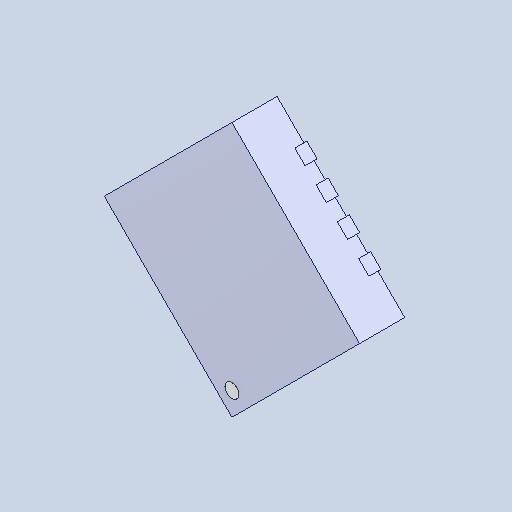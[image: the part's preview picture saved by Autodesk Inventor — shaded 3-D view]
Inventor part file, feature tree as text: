
AUTODESK INVENTOR PART (.ipt)
format: ipt  version: 2025 (Build 290162000, 162)  size: 231,936 bytes
history: native  units: mm
features: other x17, chamfer x2
ambient origin geometry x8: Origin, YZ Plane, XZ Plane, XY Plane, X Axis, Y Axis, Z Axis, Center Point
bodies: Solid1 (feature_tree), Solid2 (feature_tree), Solid3 (feature_tree), Solid4 (feature_tree), Solid5 (feature_tree), Solid6 (feature_tree), Solid7 (feature_tree), Solid8 (feature_tree), Solid9 (feature_tree), Solid10 (feature_tree), Solid11 (feature_tree), Solid12 (feature_tree), Solid13 (feature_tree), Solid14 (feature_tree), Solid15 (feature_tree), Solid16 (feature_tree), Solid17 (feature_tree), Solid18 (feature_tree), Solid19 (feature_tree)
feature tree (19):
  other  "LPattern4[4]"
  other  "LPattern3[4]"
  chamfer  "Chamfer2"  [1 undecoded]
  other  "LPattern4[1]"
  chamfer  "Chamfer1"  [1 undecoded]
  other  "Boss-Extrude2[2]"
  other  "LPattern3[3]"
  other  "LPattern4[5]"
  other  "Boss-Extrude3[2]"
  other  "LPattern3[5]"
  other  "LPattern4[3]"
  other  "LPattern3[1]"
  other  "Boss-Extrude3[1]"
  other  "LPattern4[2]"
  other  "LPattern3[6]"
  other  "LPattern3[2]"
  other  "LPattern4[6]"
  other  "Boss-Extrude2[1]"
  other  "PIN1"
note: 2 required parameter values undecoded (feature->parameter linkage not recoverable at this tier; creation-order binding heuristic only, values carry confidence <= 0.55)
